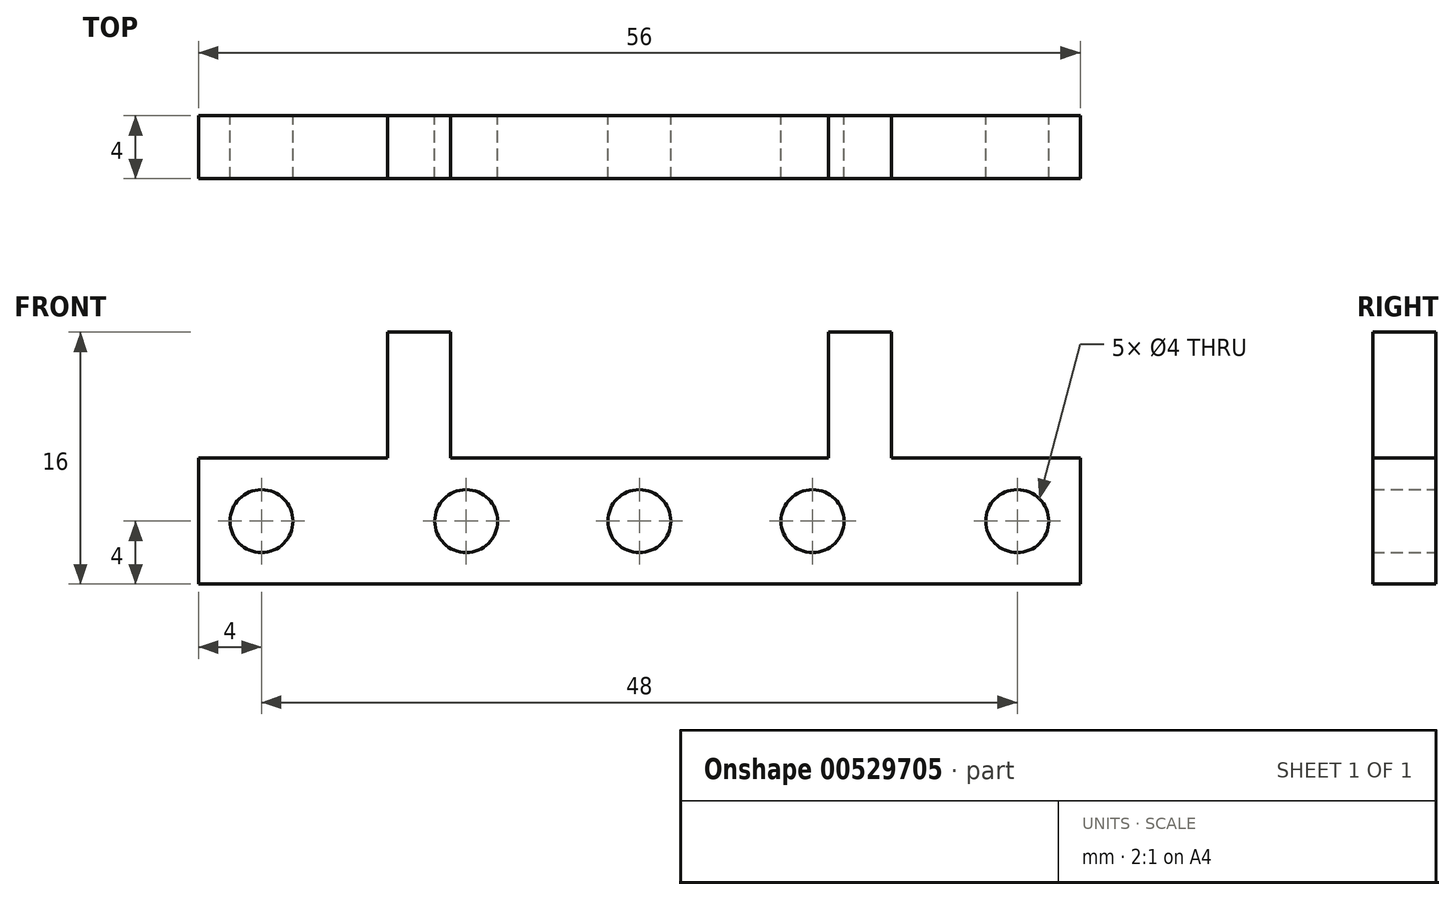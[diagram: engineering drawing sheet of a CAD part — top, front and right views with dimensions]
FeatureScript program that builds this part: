
annotation { "Feature Type Name" : "Feature", "Feature Type Description" : "" }
export const myFeature = defineFeature(function(context is Context, id is Id, definition is map)
    precondition{}
    {
        {
            var Q0;
            Q0=qCreatedBy(makeId("Front.planeOp"),FACE);
            var sketch = newSketch(context, id + "F0", { "sketchPlane" : qUnion([Q0])});
            skCircle(sketch, "E0", {"center": v(0, 0) * mm, "radius": 2 * mm});
            skCircle(sketch, "E1", {"center": v(-11, 0) * mm, "radius": 2 * mm});
            skCircle(sketch, "E2", {"center": v(-24, 0) * mm, "radius": 2 * mm});
            skLineSegment(sketch, "E3", {"start": v(-28, -4) * mm, "end": v(-28, 4) * mm});
            skLineSegment(sketch, "E4", {"start": v(-28, 4) * mm, "end": v(-16, 4) * mm});
            skLineSegment(sketch, "E5", {"start": v(-16, 4) * mm, "end": v(-16, 12) * mm});
            skLineSegment(sketch, "E6", {"start": v(-16, 12) * mm, "end": v(-12, 12) * mm});
            skLineSegment(sketch, "E7", {"start": v(-12, 12) * mm, "end": v(-12, 4) * mm});
            skLineSegment(sketch, "E8", {"start": v(-12, 4) * mm, "end": v(0, 4) * mm});
            skLineSegment(sketch, "E9.MirrorCS", {"start": v(28, 4) * mm, "end": v(16, 4) * mm});
            skLineSegment(sketch, "E10.MirrorCS", {"start": v(12, 4) * mm, "end": v(0, 4) * mm});
            skLineSegment(sketch, "E11.MirrorCS", {"start": v(16, 12) * mm, "end": v(12, 12) * mm});
            skLineSegment(sketch, "E12.MirrorCS", {"start": v(28, -4) * mm, "end": v(28, 4) * mm});
            skCircle(sketch, "E13.MirrorC", {"center": v(11, 0) * mm, "radius": 2 * mm});
            skCircle(sketch, "E14.MirrorC", {"center": v(24, 0) * mm, "radius": 2 * mm});
            skLineSegment(sketch, "E15.MirrorCS", {"start": v(16, 4) * mm, "end": v(16, 12) * mm});
            skLineSegment(sketch, "E16.MirrorCS", {"start": v(12, 12) * mm, "end": v(12, 4) * mm});
            skLineSegment(sketch, "E17", {"start": v(-28, -4) * mm, "end": v(28, -4) * mm});
            skSolve(sketch);
        }
        {
            var Q0;
            Q0 = qSketchRegion(id + "F0", true);
            extrude(context, id + "F1", {"entities" : qUnion([Q0]), "depth" : 4 * mm, "offsetDistance" : 25 * mm});
        }
    });
